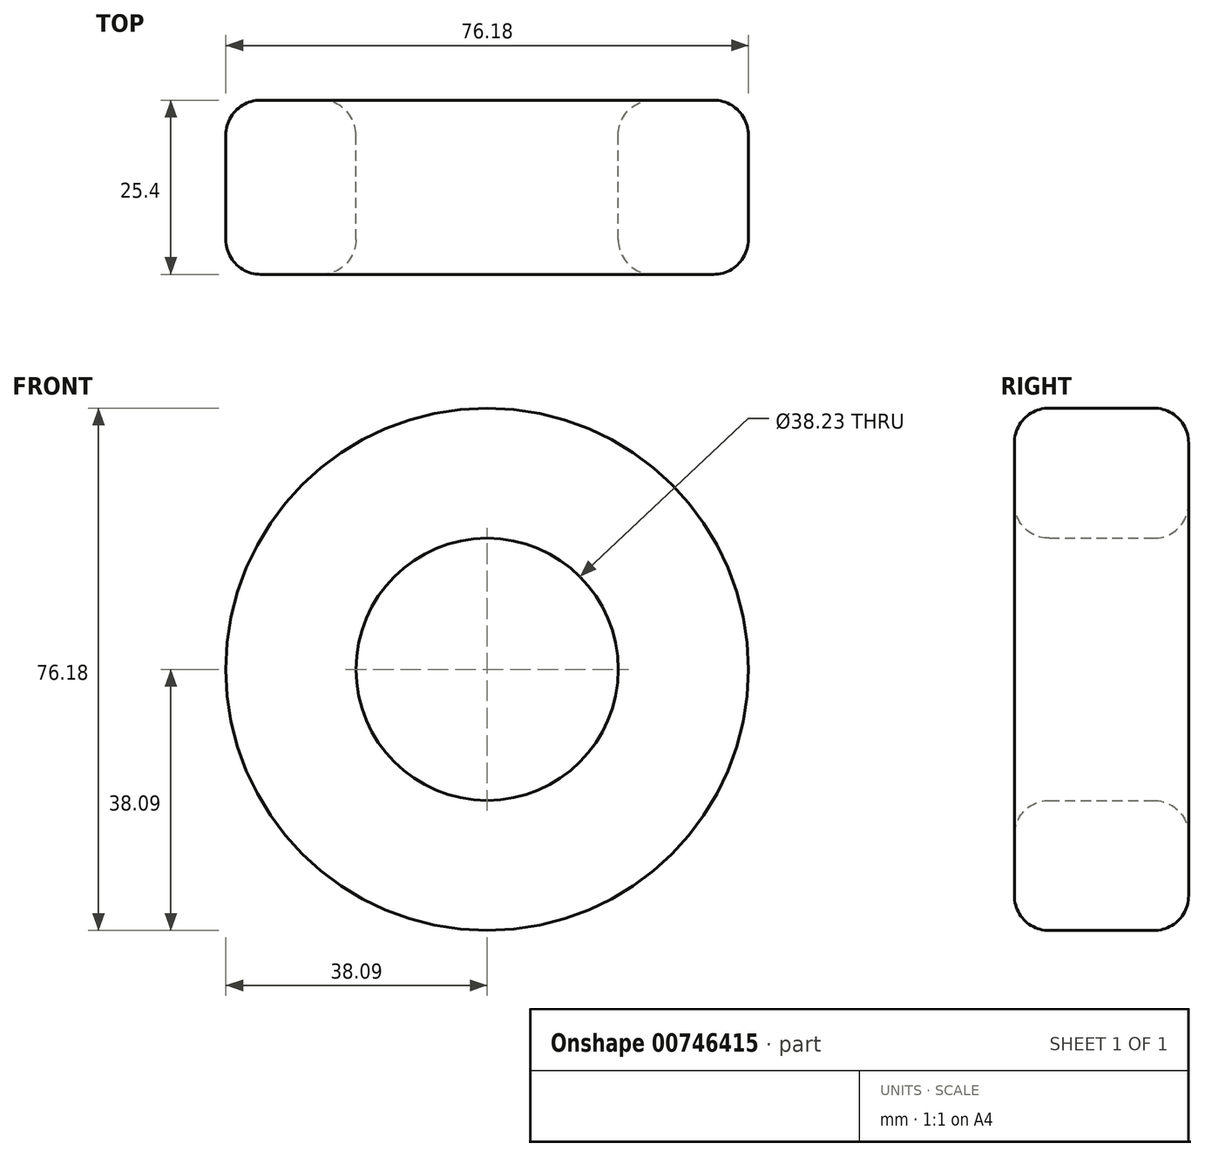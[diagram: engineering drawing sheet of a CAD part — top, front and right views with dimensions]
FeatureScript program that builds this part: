
annotation { "Feature Type Name" : "Feature", "Feature Type Description" : "" }
export const myFeature = defineFeature(function(context is Context, id is Id, definition is map)
    precondition{}
    {
        {
            var Q0;
            Q0=qCreatedBy(makeId("Front.planeOp"),FACE);
            var sketch = newSketch(context, id + "F0", { "sketchPlane" : qUnion([Q0])});
            skCircle(sketch, "E0", {"center": v(0, 0) * mm, "radius": 38.1 * mm});
            skCircle(sketch, "E1", {"center": v(0, 0) * mm, "radius": 19.12 * mm});
            skSolve(sketch);
        }
        {
            var Q0;
            Q0=makeQuery(id+"F0.imprint","IMPRINT",FACE,{"disambiguationData":[TD([[makeQuery(id+"F0.imprint","IMPRINT",EDGE,{"derivedFrom":sQuery(id+"F0.wireOp",EDGE,"E0")}),1.0]])]});
            extrude(context, id + "F1", {"entities" : qUnion([Q0]), "depth" : 25.4 * mm, "offsetDistance" : 25.4 * mm});
        }
        {
            var Q0;
            Q0=makeQuery(id+"F1.opExtrude","CAP_FACE",FACE,{"disambiguationData":[OSD([sQuery(id+"F0.wireOp",EDGE,"E0"),sQuery(id+"F0.wireOp",EDGE,"E1")])],"isStart":false});
            var Q1;
            Q1=makeQuery(id+"F1.opExtrude","CAP_FACE",FACE,{"disambiguationData":[OSD([sQuery(id+"F0.wireOp",EDGE,"E0"),sQuery(id+"F0.wireOp",EDGE,"E1")])],"isStart":true});
            fillet(context, id + "F2", {"entities" : qUnion([Q0, Q1]), "radius" : 5.08 * mm, "tangentPropagation" : true, "allowEdgeOverflow" : false});
        }
    });
